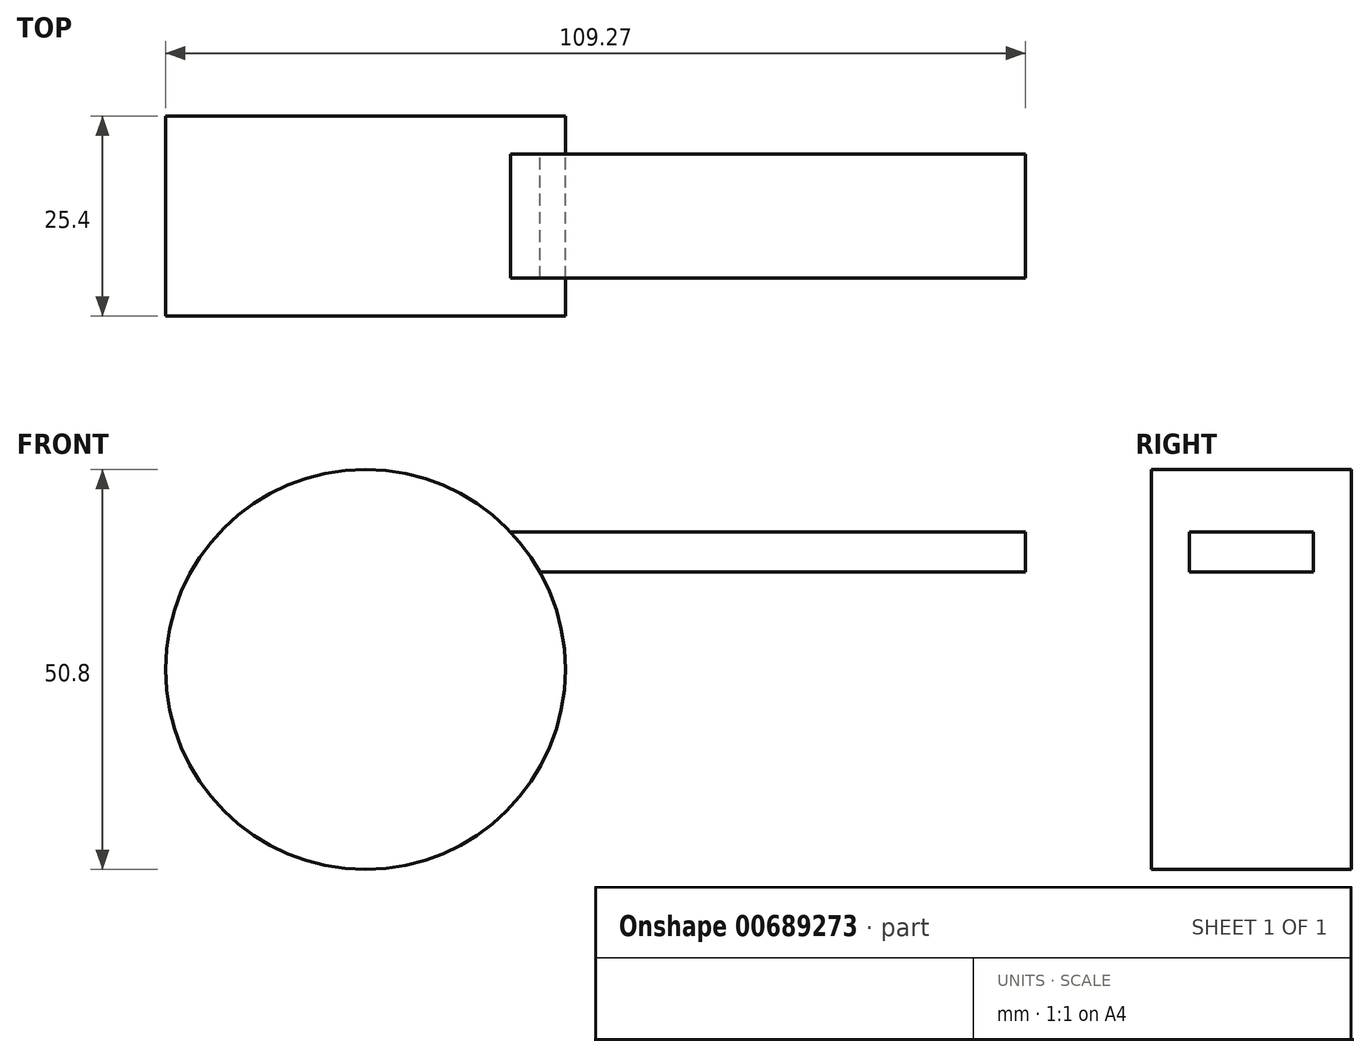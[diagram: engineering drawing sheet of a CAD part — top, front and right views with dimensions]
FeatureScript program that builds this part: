
annotation { "Feature Type Name" : "Feature", "Feature Type Description" : "" }
export const myFeature = defineFeature(function(context is Context, id is Id, definition is map)
    precondition{}
    {
        {
            var Q0;
            Q0=qCreatedBy(makeId("Front.planeOp"),FACE);
            var sketch = newSketch(context, id + "F0", { "sketchPlane" : qUnion([Q0])});
            skCircle(sketch, "E0", {"center": v(-33.07, 16.15) * mm, "radius": 25.4 * mm});
            skSolve(sketch);
        }
        {
            var Q0;
            Q0=makeQuery(id+"F0.imprint","IMPRINT",FACE,{"disambiguationData":[TD([[makeQuery(id+"F0.imprint","IMPRINT",EDGE,{"derivedFrom":sQuery(id+"F0.wireOp",EDGE,"E0")}),1.0]])]});
            extrude(context, id + "F1", {"entities" : qUnion([Q0]), "depth" : 25.4 * mm, "offsetDistance" : 25.4 * mm});
        }
        {
            var Q0;
            Q0=qCreatedBy(makeId("Right.planeOp"),FACE);
            var sketch = newSketch(context, id + "F2", { "sketchPlane" : qUnion([Q0])});
            skLineSegment(sketch, "E1.bottom", {"start": v(-20.57, 33.6) * mm, "end": v(-4.83, 33.6) * mm});
            skLineSegment(sketch, "E1.top", {"start": v(-20.57, 28.52) * mm, "end": v(-4.83, 28.52) * mm});
            skLineSegment(sketch, "E1.left", {"start": v(-20.57, 33.6) * mm, "end": v(-20.57, 28.52) * mm});
            skLineSegment(sketch, "E1.right", {"start": v(-4.83, 33.6) * mm, "end": v(-4.83, 28.52) * mm});
            skSolve(sketch);
        }
        {
            var Q0;
            Q0=makeQuery(id+"F2.imprint","IMPRINT",FACE,{"disambiguationData":[TD([[makeQuery(id+"F2.imprint","IMPRINT",EDGE,{"derivedFrom":sQuery(id+"F2.wireOp",EDGE,"E1.bottom")}),-1.0]])]});
            extrude(context, id + "F3", {"entities" : qUnion([Q0]), "operationType" : NewBodyOperationType.ADD, "depth" : 50.8 * mm, "offsetDistance" : 25.4 * mm, "hasSecondDirection" : true, "secondDirectionOppositeDirection" : true, "secondDirectionDepth" : 25.4 * mm});
        }
    });
